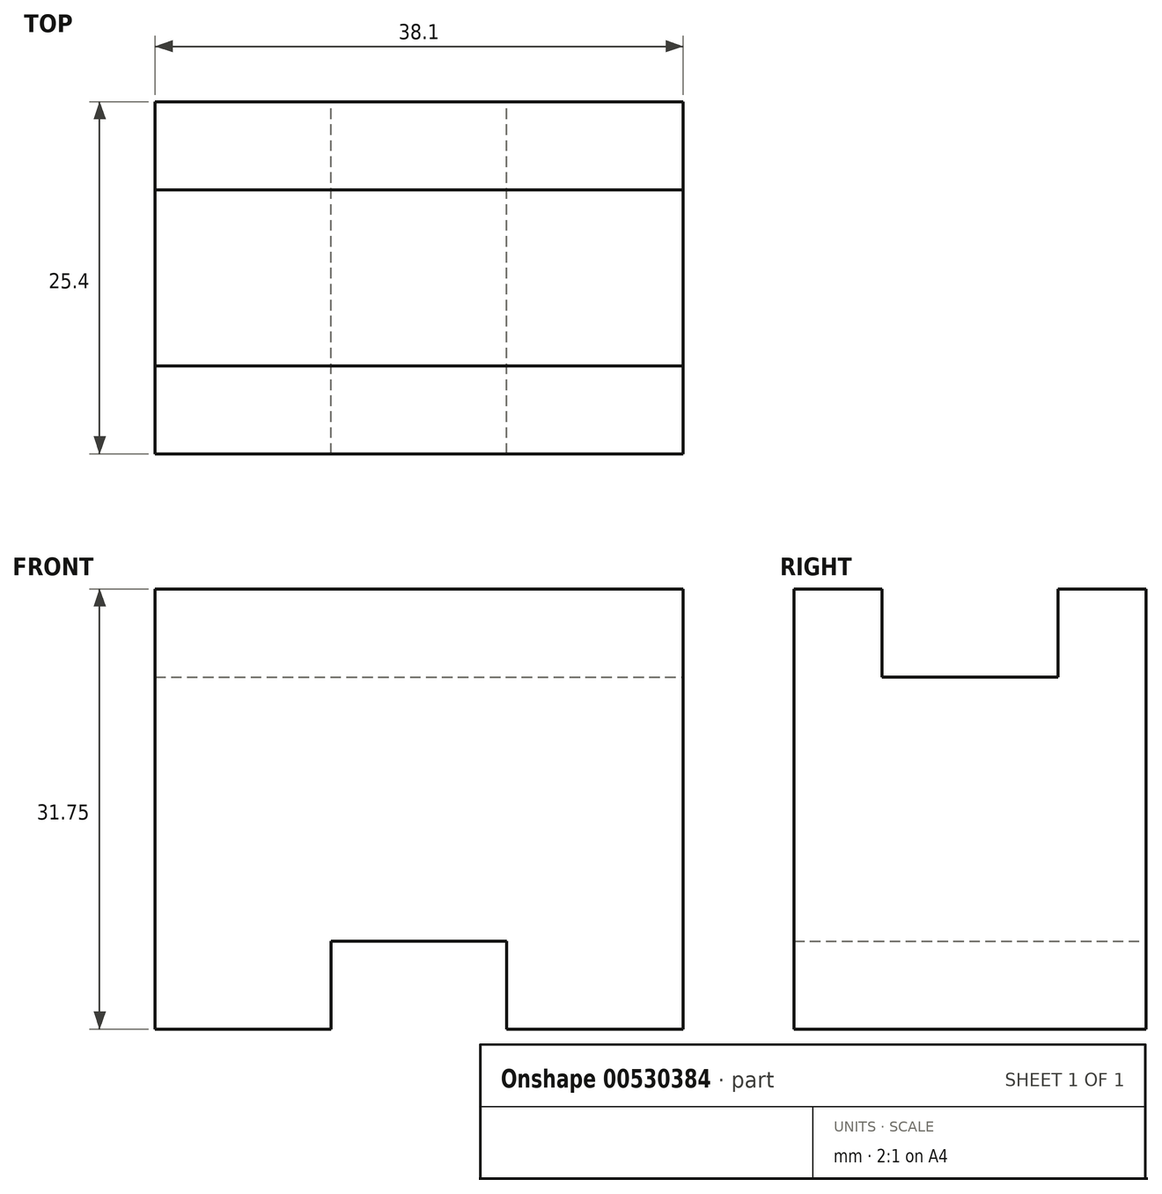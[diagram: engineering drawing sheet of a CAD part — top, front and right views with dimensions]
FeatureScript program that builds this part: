
annotation { "Feature Type Name" : "Feature", "Feature Type Description" : "" }
export const myFeature = defineFeature(function(context is Context, id is Id, definition is map)
    precondition{}
    {
        {
            var Q0;
            Q0=qCreatedBy(makeId("Front.planeOp"),FACE);
            var sketch = newSketch(context, id + "F0", { "sketchPlane" : qUnion([Q0])});
            skLineSegment(sketch, "E0", {"start": v(-25.35, 31.75) * mm, "end": v(-25.35, 0) * mm});
            skLineSegment(sketch, "E1", {"start": v(-25.35, 0) * mm, "end": v(12.75, 0) * mm});
            skLineSegment(sketch, "E2", {"start": v(12.75, 0) * mm, "end": v(12.75, 31.75) * mm});
            skLineSegment(sketch, "E3", {"start": v(12.75, 31.75) * mm, "end": v(-25.35, 31.75) * mm});
            skSolve(sketch);
        }
        {
            var Q0;
            Q0=makeQuery(id+"F0.imprint","IMPRINT",FACE,{"disambiguationData":[TD([[makeQuery(id+"F0.imprint","IMPRINT",EDGE,{"derivedFrom":sQuery(id+"F0.wireOp",EDGE,"E0")}),1.0]])]});
            extrude(context, id + "F1", {"entities" : qUnion([Q0]), "depth" : 25.4 * mm, "offsetDistance" : 25.4 * mm});
        }
        {
            var Q0;
            Q0=makeQuery(id+"F1.opExtrude","SWEPT_FACE",FACE,{"disambiguationData":[OSD([sQuery(id+"F0.wireOp",EDGE,"E2")])]});
            var sketch = newSketch(context, id + "F2", { "sketchPlane" : qUnion([Q0])});
            skLineSegment(sketch, "E4", {"start": v(-19.05, 31.75) * mm, "end": v(-19.05, 25.4) * mm});
            skLineSegment(sketch, "E5", {"start": v(-19.05, 25.4) * mm, "end": v(-6.35, 25.4) * mm});
            skLineSegment(sketch, "E6", {"start": v(-6.35, 25.4) * mm, "end": v(-6.35, 31.75) * mm});
            skLineSegment(sketch, "E7", {"start": v(-6.35, 31.75) * mm, "end": v(-19.05, 31.75) * mm});
            skLineSegment(sketch, "E8", {"start": v(-19.05, 31.75) * mm, "end": v(-25.4, 31.75) * mm});
            skLineSegment(sketch, "E9", {"start": v(-6.35, 31.75) * mm, "end": v(0, 31.75) * mm});
            skSolve(sketch);
        }
        {
            var Q0;
            Q0=makeQuery(id+"F2.imprint","IMPRINT",FACE,{"disambiguationData":[TD([[makeQuery(id+"F2.imprint","IMPRINT",EDGE,{"derivedFrom":sQuery(id+"F2.wireOp",EDGE,"E4")}),1.0]])]});
            extrude(context, id + "F3", {"entities" : qUnion([Q0]), "operationType" : NewBodyOperationType.REMOVE, "endBound" : BoundingType.THROUGH_ALL, "oppositeDirection" : true, "depth" : 25.4 * mm, "offsetDistance" : 25.4 * mm});
        }
        {
            var Q0;
            Q0=makeQuery(id+"F1.opExtrude","CAP_FACE",FACE,{"disambiguationData":[OSD([sQuery(id+"F0.wireOp",EDGE,"E0"),sQuery(id+"F0.wireOp",EDGE,"E1"),sQuery(id+"F0.wireOp",EDGE,"E2"),sQuery(id+"F0.wireOp",EDGE,"E3")])],"isStart":true});
            var sketch = newSketch(context, id + "F4", { "sketchPlane" : qUnion([Q0])});
            skLineSegment(sketch, "E10", {"start": v(0, 0) * mm, "end": v(0, 6.35) * mm});
            skLineSegment(sketch, "E11", {"start": v(-0.05, 6.35) * mm, "end": v(12.65, 6.35) * mm});
            skLineSegment(sketch, "E12", {"start": v(12.65, 6.35) * mm, "end": v(12.65, 0) * mm});
            skLineSegment(sketch, "E13", {"start": v(12.65, 0) * mm, "end": v(0, 0) * mm});
            skLineSegment(sketch, "E14", {"start": v(0, 0) * mm, "end": v(-12.75, 0) * mm});
            skLineSegment(sketch, "E15", {"start": v(12.65, 0) * mm, "end": v(25.35, 0) * mm});
            skSolve(sketch);
        }
        {
            var Q0;
            {var subQ0=sQuery(id+"F4.wireOp",EDGE,"E10");Q0=makeQuery(id+"F4.imprint","IMPRINT",FACE,{"disambiguationData":[TD([[makeQuery(id+"F4.imprint","IMPRINT",EDGE,{"derivedFrom":subQ0}),-1.0]])]});}
            extrude(context, id + "F5", {"entities" : qUnion([Q0]), "operationType" : NewBodyOperationType.REMOVE, "endBound" : BoundingType.THROUGH_ALL, "oppositeDirection" : true, "depth" : 25.4 * mm, "offsetDistance" : 25.4 * mm});
        }
    });
